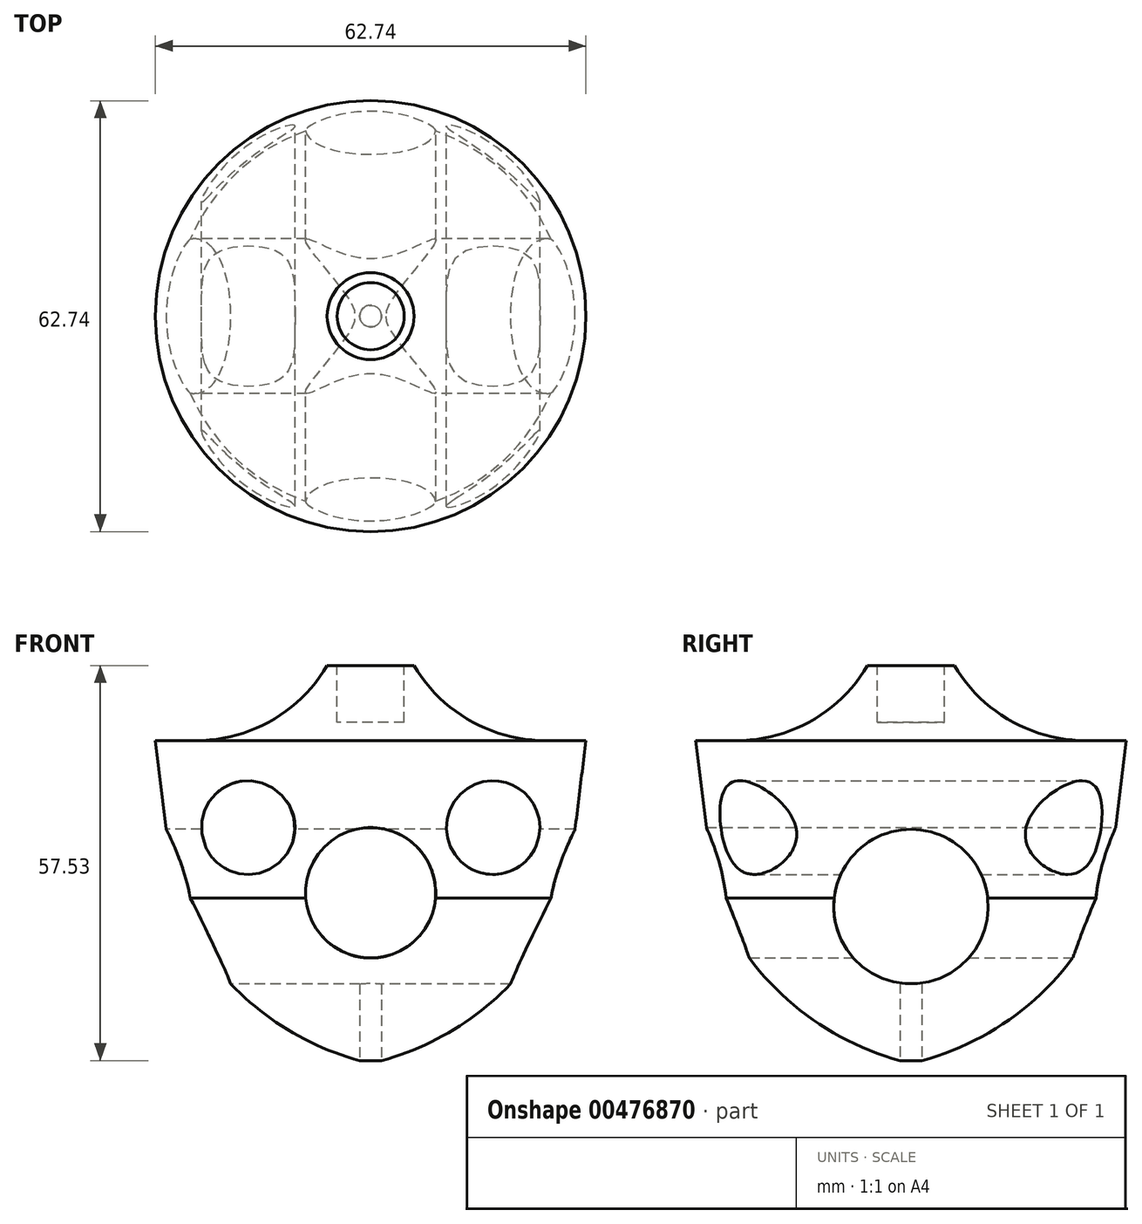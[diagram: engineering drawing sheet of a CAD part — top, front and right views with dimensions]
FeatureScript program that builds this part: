
annotation { "Feature Type Name" : "Feature", "Feature Type Description" : "" }
export const myFeature = defineFeature(function(context is Context, id is Id, definition is map)
    precondition{}
    {
        {
            var Q0;
            Q0=qCreatedBy(makeId("Front.planeOp"),FACE);
            var sketch = newSketch(context, id + "F0", { "sketchPlane" : qUnion([Q0])});
            skLineSegment(sketch, "E0", {"start": v(0, 0) * mm, "end": v(0, 10.92) * mm});
            skLineSegment(sketch, "E1", {"start": v(0, 0) * mm, "end": v(0, -47) * mm});
            skLineSegment(sketch, "E2", {"start": v(-25.46, 0) * mm, "end": v(-25.46, 0) * mm});
            skLineSegment(sketch, "E3", {"start": v(-6.33, 10.94) * mm, "end": v(0, 10.92) * mm});
            skArc(sketch, "E4", {"start": v(-25.46, 0) * mm, "mid": v(-14.44, 2.93) * mm, "end": v(-6.33, 10.94) * mm});
            skPoint(sketch, "E5.endSnap0", {"position": v(0, -23.5) * mm});
            skLineSegment(sketch, "E6", {"start": v(-31.37, 0) * mm, "end": v(-28.56, -22.9) * mm});
            skArc(sketch, "E7", {"start": v(-28.56, -22.9) * mm, "mid": v(-17.2, -38.42) * mm, "end": v(0, -47) * mm});
            skLineSegment(sketch, "E8", {"start": v(-25.46, 0) * mm, "end": v(-31.37, 0) * mm});
            skSolve(sketch);
        }
        {
            var Q0;
            Q0=makeQuery(id+"F0.imprint","IMPRINT",FACE,{"disambiguationData":[TD([[makeQuery(id+"F0.imprint","IMPRINT",EDGE,{"derivedFrom":sQuery(id+"F0.wireOp",EDGE,"E1")}),-1.0]])]});
            var Q1;
            {var subQ0=sQuery(id+"F0.wireOp",EDGE,"E0");Q1=makeQuery(id+"F0.imprint","IMPRINT",FACE,{"disambiguationData":[TD([[makeQuery(id+"F0.imprint","IMPRINT",EDGE,{"derivedFrom":subQ0}),1.0]])]});}
            var Q2;
            Q2=sQuery(id+"F0.wireOp",EDGE,"E2");
            var Q3;
            Q3=sQuery(id+"F0.wireOp",EDGE,"ea7b3b8c-bd75-4244-b75b-0336513395d12");
            var Q4;
            Q4=sQuery(id+"F0.wireOp",EDGE,"7MbwPrU4-QeTn-B9Gg-FLhE-dXKIEwnGr0nX");
            var Q5;
            Q5=sQuery(id+"F0.wireOp",EDGE,"E3");
            var Q6;
            Q6=sQuery(id+"F0.wireOp",EDGE,"E0");
            var Q7;
            Q7=sQuery(id+"F0.wireOp",EDGE,"E1");
            var Q8;
            Q8=sQuery(id+"F0.wireOp",EDGE,"E1");
            revolve(context, id + "F1", {"entities" : qUnion([Q0, Q1]), "surfaceEntities" : qUnion([Q2, Q3, Q4, Q5, Q6, Q7]), "axis" : qUnion([Q8]), "revolveType" : RevolveType.FULL});
        }
        {
            var Q0;
            Q0=qCreatedBy(makeId("Front.planeOp"),FACE);
            var sketch = newSketch(context, id + "F2", { "sketchPlane" : qUnion([Q0])});
            skCircle(sketch, "E9", {"center": v(0, -22.16) * mm, "radius": 9.5 * mm});
            skCircle(sketch, "E10", {"center": v(17.84, -12.66) * mm, "radius": 6.82 * mm});
            skCircle(sketch, "E11.MirrorC", {"center": v(-17.84, -12.66) * mm, "radius": 6.82 * mm});
            skSolve(sketch);
        }
        {
            var Q0;
            Q0=qSketchRegion(id+"F2",true);
            extrude(context, id + "F3", {"entities" : qUnion([Q0]), "operationType" : NewBodyOperationType.REMOVE, "depth" : 254 * mm, "hasSecondDirection" : true, "secondDirectionOppositeDirection" : true, "secondDirectionDepth" : 254 * mm});
        }
        {
            var Q0;
            Q0=qCreatedBy(makeId("Right.planeOp"),FACE);
            var sketch = newSketch(context, id + "F4", { "sketchPlane" : qUnion([Q0])});
            skCircle(sketch, "E12", {"center": v(0, -24.18) * mm, "radius": 11.26 * mm});
            skSolve(sketch);
        }
        {
            var Q0;
            Q0=qSketchRegion(id+"F4",true);
            extrude(context, id + "F5", {"entities" : qUnion([Q0]), "operationType" : NewBodyOperationType.REMOVE, "depth" : 254 * mm, "hasSecondDirection" : true, "secondDirectionOppositeDirection" : true, "secondDirectionDepth" : 254 * mm});
        }
        {
            var Q0;
            Q0=qCreatedBy(makeId("Top.planeOp"),FACE);
            cPlane(context, id + "F6", {"entities" : qUnion([Q0]), "cplaneType" : CPlaneType.OFFSET, "offset" : 47 * mm, "oppositeDirection" : true, "width" : 152.4 * mm, "height" : 152.4 * mm});
        }
        {
            var Q0;
            Q0=qCreatedBy(makeId("Top.planeOp"),FACE);
            cPlane(context, id + "F7", {"entities" : qUnion([Q0]), "cplaneType" : CPlaneType.OFFSET, "offset" : 10.92 * mm, "width" : 152.4 * mm, "height" : 152.4 * mm});
        }
        {
            var Q0;
            Q0=qCreatedBy(id+"F7.planeOp",FACE);
            var sketch = newSketch(context, id + "F8", { "sketchPlane" : qUnion([Q0])});
            skCircle(sketch, "E13", {"center": v(0, 0) * mm, "radius": 4.89 * mm});
            skSolve(sketch);
        }
        {
            var Q0;
            Q0=makeQuery(id+"F8.imprint","IMPRINT",FACE,{"disambiguationData":[TD([[makeQuery(id+"F8.imprint","IMPRINT",EDGE,{"derivedFrom":sQuery(id+"F8.wireOp",EDGE,"E13")}),1.0]])]});
            extrude(context, id + "F9", {"entities" : qUnion([Q0]), "operationType" : NewBodyOperationType.REMOVE, "oppositeDirection" : true, "depth" : 8.25 * mm, "hasSecondDirection" : true, "secondDirectionOppositeDirection" : false, "secondDirectionDepth" : 82.55 * mm});
        }
        {
            var Q0;
            Q0=qCreatedBy(id+"F6.planeOp",FACE);
            var sketch = newSketch(context, id + "F10", { "sketchPlane" : qUnion([Q0])});
            skCircle(sketch, "E14", {"center": v(0, 0) * mm, "radius": 1.59 * mm});
            skSolve(sketch);
        }
        {
            var Q0;
            Q0=qSketchRegion(id+"F10",true);
            extrude(context, id + "F11", {"entities" : qUnion([Q0]), "operationType" : NewBodyOperationType.REMOVE, "depth" : 25.4 * mm, "hasSecondDirection" : true, "secondDirectionOppositeDirection" : true, "secondDirectionDepth" : 14.29 * mm});
        }
    });
